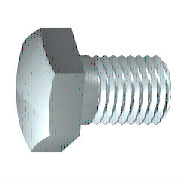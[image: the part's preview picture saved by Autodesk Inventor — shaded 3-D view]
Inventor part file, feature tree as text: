
AUTODESK INVENTOR PART (.ipt)
format: ipt  version: 2025.1 (Build 291241020, 241B)  size: 196,608 bytes
history: native  units: mm (DEFAULTED — no unit token found)
features: extrude x1, chamfer x1, plane x1
ambient origin geometry x7: Origin, YZ Plane, XZ Plane, X Axis, Y Axis, Z Axis, Center Point
bodies: Solid1 (feature_tree), Body (feature_tree)
feature tree (3):
  extrude  "Head"  Depth=50.0mm
  chamfer  "Chamfer1"  Distance=30.0mm
  plane  "Work Plane1"
